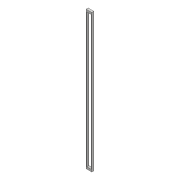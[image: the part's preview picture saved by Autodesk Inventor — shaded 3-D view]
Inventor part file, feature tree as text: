
AUTODESK INVENTOR PART (.ipt)
format: ipt  version: 2017 (Build 210142000, 142)  size: 91,648 bytes
history: native  units: mm
features: extrude x3, sketch x3
ambient origin geometry x8: Origin, YZ Plane, XZ Plane, XY Plane, X Axis, Y Axis, Z Axis, Center Point
bodies: Solid1 (feature_tree)
feature tree (6):
  extrude  "Extrusion1"  Depth=10.0mm
  extrude  "Extrusion2"  Depth=10.0mm TaperAngle=0.0deg
  extrude  "Extrusion3"  [1 undecoded]
  sketch  "Sketch1"  dims[d0=4.0mm d1=10.0mm]
  sketch  "Sketch2"  dims[d3=650.0mm d4=0.0mm d5=10.0mm d6=0.0mm]
  sketch  "Sketch3"  dims[d7=10.0mm d8=0.0mm]
note: 1 required parameter value undecoded (feature->parameter linkage not recoverable at this tier; creation-order binding heuristic only, values carry confidence <= 0.55)
